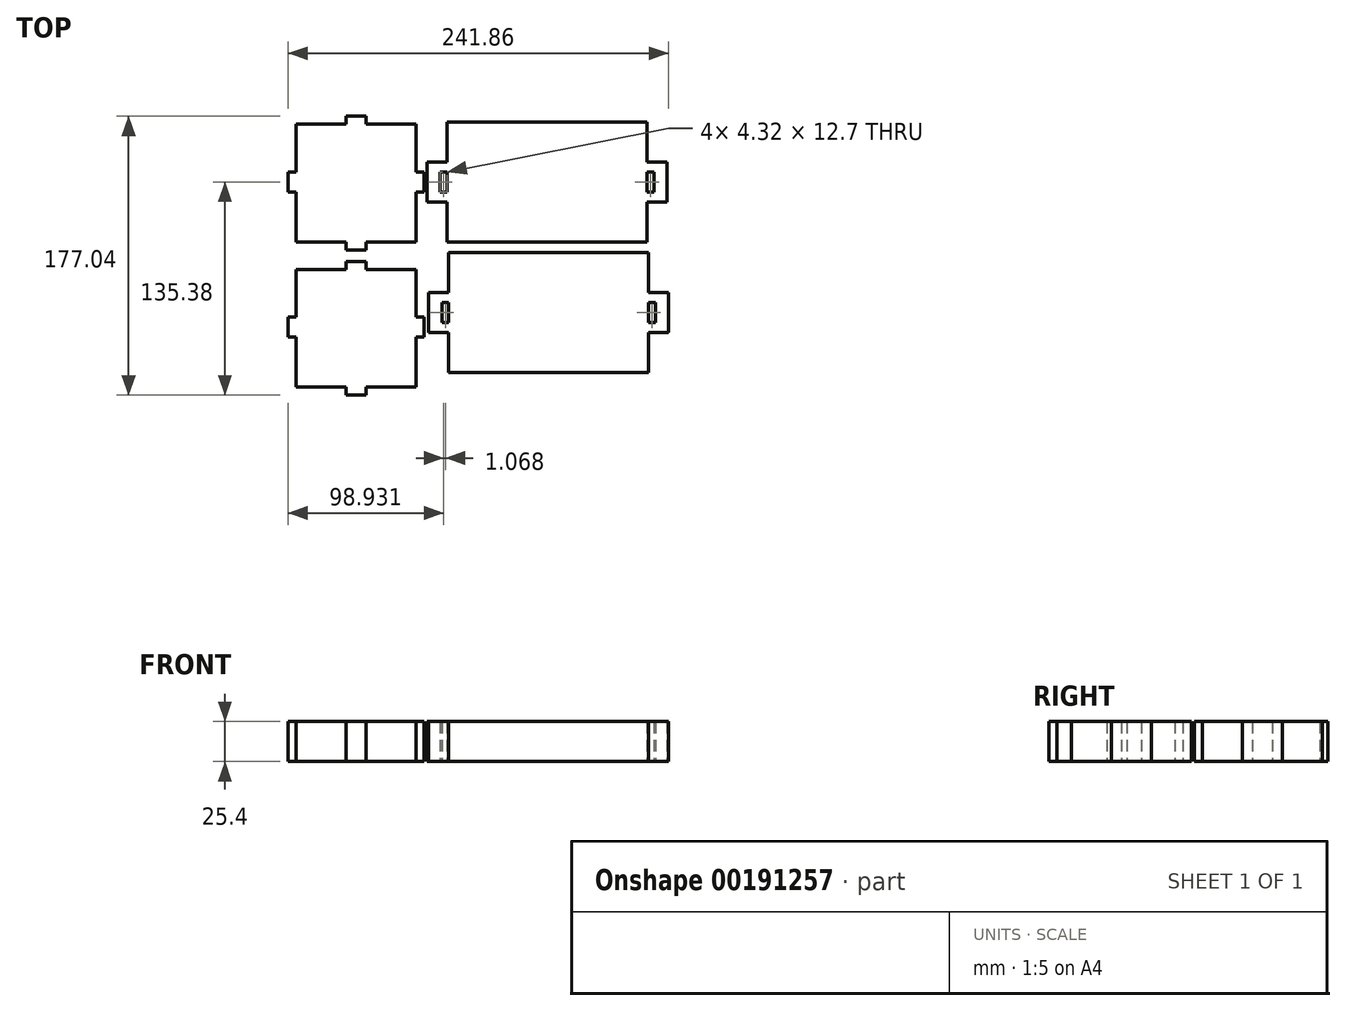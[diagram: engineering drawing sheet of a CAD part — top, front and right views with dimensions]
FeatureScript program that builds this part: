
annotation { "Feature Type Name" : "Feature", "Feature Type Description" : "" }
export const myFeature = defineFeature(function(context is Context, id is Id, definition is map)
    precondition{}
    {
        {
            var Q0;
            Q0=qCreatedBy(makeId("Top.planeOp"),FACE);
            var sketch = newSketch(context, id + "F0", { "sketchPlane" : qUnion([Q0])});
            skLineSegment(sketch, "E0.top", {"start": v(-63.5, 38.1) * mm, "end": v(63.5, 38.1) * mm});
            skPoint(sketch, "E1.0.1.0", {"position": v(-63.5, 88.9) * mm});
            skPoint(sketch, "E1.0.1.1", {"position": v(-76.2, 63.5) * mm});
            skPoint(sketch, "E1.0.1.2", {"position": v(69.85, 63.5) * mm});
            skPoint(sketch, "E1.0.1.3", {"position": v(-76.2, 76.2) * mm});
            skPoint(sketch, "E1.0.1.5", {"position": v(76.2, 76.2) * mm});
            skLineSegment(sketch, "E1.0.1.6", {"start": v(-63.5, 38.1) * mm, "end": v(-63.5, 114.3) * mm});
            skLineSegment(sketch, "E1.0.1.7", {"start": v(63.5, 38.1) * mm, "end": v(63.5, 114.3) * mm});
            skPoint(sketch, "E1.0.1.8", {"position": v(66.04, 69.85) * mm});
            skPoint(sketch, "E1.0.1.9", {"position": v(63.5, 76.2) * mm});
            skPoint(sketch, "E1.0.1.10", {"position": v(-73.15, 88.9) * mm});
            skLineSegment(sketch, "E1.0.1.11", {"start": v(-63.5, 63.5) * mm, "end": v(-76.2, 63.5) * mm});
            skPoint(sketch, "E1.0.1.12", {"position": v(0, 76.2) * mm});
            skLineSegment(sketch, "E1.0.1.13", {"start": v(63.5, 88.9) * mm, "end": v(76.2, 88.9) * mm});
            skLineSegment(sketch, "E1.0.1.14", {"start": v(-63.5, 114.3) * mm, "end": v(63.5, 114.3) * mm});
            skLineSegment(sketch, "E1.0.1.15", {"start": v(69.85, 82.55) * mm, "end": v(69.85, 69.85) * mm});
            skPoint(sketch, "E1.0.1.16", {"position": v(76.2, 88.9) * mm});
            skPoint(sketch, "E1.0.1.17", {"position": v(-63.5, 76.2) * mm});
            skPoint(sketch, "E1.0.1.18", {"position": v(63.5, 88.9) * mm});
            skPoint(sketch, "E1.0.1.19", {"position": v(76.2, 63.5) * mm});
            skLineSegment(sketch, "E1.0.1.20", {"start": v(-69.85, 82.55) * mm, "end": v(-69.85, 69.85) * mm});
            skPoint(sketch, "E1.0.1.21", {"position": v(76.2, 76.2) * mm});
            skLineSegment(sketch, "E1.0.1.22", {"start": v(-63.5, 114.3) * mm, "end": v(63.5, 114.3) * mm});
            skLineSegment(sketch, "E1.0.1.23", {"start": v(76.2, 88.9) * mm, "end": v(76.2, 63.5) * mm});
            skLineSegment(sketch, "E1.0.1.24", {"start": v(-76.2, 88.9) * mm, "end": v(-76.2, 63.5) * mm});
            skPoint(sketch, "E1.0.1.25", {"position": v(-69.85, 88.9) * mm});
            skPoint(sketch, "E1.0.1.26", {"position": v(63.5, 76.2) * mm});
            skLineSegment(sketch, "E1.0.1.27", {"start": v(63.5, 63.5) * mm, "end": v(76.2, 63.5) * mm});
            skLineSegment(sketch, "E1.0.1.28", {"start": v(-63.5, 76.2) * mm, "end": v(-63.5, 69.85) * mm});
            skLineSegment(sketch, "E1.0.1.29", {"start": v(-63.5, 82.55) * mm, "end": v(-69.85, 82.55) * mm});
            skLineSegment(sketch, "E1.0.1.30", {"start": v(-63.5, 69.85) * mm, "end": v(-69.85, 69.85) * mm});
            skLineSegment(sketch, "E1.0.1.31", {"start": v(-63.5, 88.9) * mm, "end": v(-76.2, 88.9) * mm});
            skLineSegment(sketch, "E1.0.1.32", {"start": v(-63.5, 88.9) * mm, "end": v(-63.5, 63.5) * mm});
            skLineSegment(sketch, "E1.0.1.33", {"start": v(63.5, 76.2) * mm, "end": v(63.5, 82.55) * mm});
            skLineSegment(sketch, "E1.0.1.34", {"start": v(63.5, 69.85) * mm, "end": v(69.85, 69.85) * mm});
            skLineSegment(sketch, "E1.0.1.35", {"start": v(63.5, 82.55) * mm, "end": v(69.85, 82.55) * mm});
            skLineSegment(sketch, "E1.0.1.36", {"start": v(63.5, 88.9) * mm, "end": v(63.5, 63.5) * mm});
            skLineSegment(sketch, "E1.0.1.37", {"start": v(63.5, 82.55) * mm, "end": v(63.5, 69.85) * mm});
            skLineSegment(sketch, "E1.0.1.38", {"start": v(-63.5, 76.2) * mm, "end": v(-63.5, 82.55) * mm});
            skLineSegment(sketch, "E1.0.1.39", {"start": v(-63.5, 82.55) * mm, "end": v(-63.5, 69.85) * mm});
            skPoint(sketch, "E2", {"position": v(76.2, 82.55) * mm});
            skPoint(sketch, "E3", {"position": v(68.26, 82.55) * mm});
            skLineSegment(sketch, "E4", {"start": v(68.26, 69.85) * mm, "end": v(69.85, 69.85) * mm});
            skPoint(sketch, "E5", {"position": v(67.82, 82.55) * mm});
            skLineSegment(sketch, "E6.top", {"start": v(71.1, 69.85) * mm, "end": v(66.04, 69.85) * mm});
            skLineSegment(sketch, "E7", {"start": v(67.82, 82.55) * mm, "end": v(67.82, 69.85) * mm});
            skPoint(sketch, "E8", {"position": v(-67.82, 69.85) * mm});
            skLineSegment(sketch, "E9", {"start": v(-67.82, 69.85) * mm, "end": v(-67.82, 82.55) * mm});
            skPoint(sketch, "E10", {"position": v(-78.23, 88.9) * mm});
            skPoint(sketch, "E11", {"position": v(-78.23, 82.55) * mm});
            skPoint(sketch, "E12", {"position": v(-78.23, 69.85) * mm});
            skPoint(sketch, "E13", {"position": v(-83.31, 82.55) * mm});
            skLineSegment(sketch, "E14.bottom", {"start": v(-83.31, 82.55) * mm, "end": v(-78.23, 82.55) * mm});
            skLineSegment(sketch, "E14.top", {"start": v(-83.31, 69.85) * mm, "end": v(-78.23, 69.85) * mm});
            skLineSegment(sketch, "E14.left", {"start": v(-83.31, 82.55) * mm, "end": v(-83.31, 69.85) * mm});
            skLineSegment(sketch, "E14.right", {"start": v(-78.23, 82.55) * mm, "end": v(-78.23, 69.85) * mm});
            skPoint(sketch, "E15", {"position": v(-170.57, 59.84) * mm});
            skLineSegment(sketch, "E16.bottom", {"start": v(-83.31, 38.1) * mm, "end": v(-159.51, 38.1) * mm});
            skLineSegment(sketch, "E16.top", {"start": v(-83.31, 112.78) * mm, "end": v(-159.51, 112.78) * mm});
            skLineSegment(sketch, "E16.left", {"start": v(-83.31, 38.1) * mm, "end": v(-83.31, 112.78) * mm});
            skLineSegment(sketch, "E16.right", {"start": v(-159.51, 38.1) * mm, "end": v(-159.51, 112.78) * mm});
            skPoint(sketch, "E17", {"position": v(-115.06, 38.1) * mm});
            skPoint(sketch, "E18", {"position": v(-127.76, 38.1) * mm});
            skLineSegment(sketch, "E19", {"start": v(-127.76, 38.1) * mm, "end": v(-127.76, 33.02) * mm});
            skLineSegment(sketch, "E20", {"start": v(-127.76, 33.02) * mm, "end": v(-115.06, 33.02) * mm});
            skLineSegment(sketch, "E21", {"start": v(-115.06, 33.02) * mm, "end": v(-115.06, 38.1) * mm});
            skPoint(sketch, "E22", {"position": v(-159.51, 69.85) * mm});
            skPoint(sketch, "E23", {"position": v(-159.51, 82.55) * mm});
            skLineSegment(sketch, "E24", {"start": v(-159.51, 82.55) * mm, "end": v(-164.6, 82.55) * mm});
            skLineSegment(sketch, "E25", {"start": v(-164.6, 82.55) * mm, "end": v(-164.6, 69.85) * mm});
            skLineSegment(sketch, "E26", {"start": v(-164.6, 69.85) * mm, "end": v(-159.51, 69.85) * mm});
            skPoint(sketch, "E27", {"position": v(-127.76, 112.78) * mm});
            skPoint(sketch, "E28", {"position": v(-115.06, 112.78) * mm});
            skPoint(sketch, "E29", {"position": v(-127.76, 117.86) * mm});
            skLineSegment(sketch, "E30.bottom", {"start": v(-115.06, 112.78) * mm, "end": v(-127.76, 112.78) * mm});
            skLineSegment(sketch, "E30.top", {"start": v(-115.06, 117.86) * mm, "end": v(-127.76, 117.86) * mm});
            skLineSegment(sketch, "E30.left", {"start": v(-115.06, 112.78) * mm, "end": v(-115.06, 117.86) * mm});
            skLineSegment(sketch, "E30.right", {"start": v(-127.76, 112.78) * mm, "end": v(-127.76, 117.86) * mm});
            skLineSegment(sketch, "E31.direction1", {"start": v(-159.51, 38.1) * mm, "end": v(-134.11, 38.1) * mm, "construction": true});
            skPoint(sketch, "E32.0.1.0", {"position": v(68.89, -0.5) * mm});
            skPoint(sketch, "E32.0.1.1", {"position": v(70.92, -19.55) * mm});
            skPoint(sketch, "E32.0.1.2", {"position": v(77.27, -19.55) * mm});
            skPoint(sketch, "E32.0.1.3", {"position": v(67.1, -13.2) * mm});
            skPoint(sketch, "E32.0.1.4", {"position": v(-68.78, 5.85) * mm});
            skPoint(sketch, "E32.0.1.5", {"position": v(-72.08, 5.85) * mm});
            skLineSegment(sketch, "E32.0.1.6", {"start": v(-62.43, -44.95) * mm, "end": v(64.57, -44.95) * mm});
            skLineSegment(sketch, "E32.0.1.7", {"start": v(64.57, -44.95) * mm, "end": v(64.57, 31.25) * mm});
            skLineSegment(sketch, "E32.0.1.8", {"start": v(-62.43, -19.55) * mm, "end": v(-75.13, -19.55) * mm});
            skPoint(sketch, "E32.0.1.9", {"position": v(64.57, 5.85) * mm});
            skPoint(sketch, "E32.0.1.11", {"position": v(-75.13, -6.85) * mm});
            skLineSegment(sketch, "E32.0.1.12", {"start": v(-68.78, -0.5) * mm, "end": v(-68.78, -13.2) * mm});
            skLineSegment(sketch, "E32.0.1.13", {"start": v(-62.43, 31.25) * mm, "end": v(64.57, 31.25) * mm});
            skLineSegment(sketch, "E32.0.1.14", {"start": v(77.27, 5.85) * mm, "end": v(77.27, -19.55) * mm});
            skLineSegment(sketch, "E32.0.1.15", {"start": v(-75.13, 5.85) * mm, "end": v(-75.13, -19.55) * mm});
            skPoint(sketch, "E32.0.1.16", {"position": v(64.57, -6.85) * mm});
            skPoint(sketch, "E32.0.1.17", {"position": v(77.27, -0.5) * mm});
            skPoint(sketch, "E32.0.1.18", {"position": v(77.27, -6.85) * mm});
            skPoint(sketch, "E32.0.1.19", {"position": v(-62.43, 5.85) * mm});
            skPoint(sketch, "E32.0.1.20", {"position": v(69.33, -0.5) * mm});
            skPoint(sketch, "E32.0.1.21", {"position": v(-75.13, -19.55) * mm});
            skLineSegment(sketch, "E32.0.1.22", {"start": v(-62.43, -44.95) * mm, "end": v(-62.43, 31.25) * mm});
            skPoint(sketch, "E32.0.1.23", {"position": v(1.07, -6.85) * mm});
            skPoint(sketch, "E32.0.1.24", {"position": v(77.27, 5.85) * mm});
            skPoint(sketch, "E32.0.1.25", {"position": v(-62.43, -6.85) * mm});
            skLineSegment(sketch, "E32.0.1.26", {"start": v(64.57, -19.55) * mm, "end": v(77.27, -19.55) * mm});
            skLineSegment(sketch, "E32.0.1.27", {"start": v(64.57, 5.85) * mm, "end": v(77.27, 5.85) * mm});
            skLineSegment(sketch, "E32.0.1.28", {"start": v(-62.43, 31.25) * mm, "end": v(64.57, 31.25) * mm});
            skLineSegment(sketch, "E32.0.1.29", {"start": v(-62.43, -44.95) * mm, "end": v(64.57, -44.95) * mm});
            skPoint(sketch, "E32.0.1.30", {"position": v(64.57, -6.85) * mm});
            skPoint(sketch, "E32.0.1.31", {"position": v(77.27, -6.85) * mm});
            skLineSegment(sketch, "E32.0.1.32", {"start": v(-62.43, 5.85) * mm, "end": v(-75.13, 5.85) * mm});
            skLineSegment(sketch, "E32.0.1.33", {"start": v(-62.43, 5.85) * mm, "end": v(-62.43, -19.55) * mm});
            skLineSegment(sketch, "E32.0.1.34", {"start": v(64.57, 5.85) * mm, "end": v(64.57, -19.55) * mm});
            skLineSegment(sketch, "E32.0.1.35", {"start": v(-62.43, -44.95) * mm, "end": v(64.57, -44.95) * mm});
            skLineSegment(sketch, "E32.0.1.36", {"start": v(70.92, -0.5) * mm, "end": v(70.92, -13.2) * mm});
            skLineSegment(sketch, "E32.0.1.37", {"start": v(-62.43, -13.2) * mm, "end": v(-68.78, -13.2) * mm});
            skLineSegment(sketch, "E32.0.1.38", {"start": v(-62.43, -0.5) * mm, "end": v(-62.43, -13.2) * mm});
            skLineSegment(sketch, "E32.0.1.39", {"start": v(68.89, -0.5) * mm, "end": v(68.89, -13.2) * mm});
            skLineSegment(sketch, "E32.0.1.40", {"start": v(64.57, -0.5) * mm, "end": v(70.92, -0.5) * mm});
            skLineSegment(sketch, "E32.0.1.41", {"start": v(-62.43, -0.5) * mm, "end": v(-68.78, -0.5) * mm});
            skLineSegment(sketch, "E32.0.1.43", {"start": v(64.57, -0.5) * mm, "end": v(64.57, -13.2) * mm});
            skLineSegment(sketch, "E32.0.1.44", {"start": v(64.57, -6.85) * mm, "end": v(64.57, -0.5) * mm});
            skLineSegment(sketch, "E32.0.1.45", {"start": v(-62.43, -6.85) * mm, "end": v(-62.43, -0.5) * mm});
            skLineSegment(sketch, "E32.0.1.46", {"start": v(72.16, -13.2) * mm, "end": v(67.1, -13.2) * mm});
            skLineSegment(sketch, "E32.0.1.47", {"start": v(64.57, -13.2) * mm, "end": v(70.92, -13.2) * mm});
            skLineSegment(sketch, "E32.0.1.48", {"start": v(-62.43, -6.85) * mm, "end": v(-62.43, -13.2) * mm});
            skLineSegment(sketch, "E32.0.1.49", {"start": v(69.33, -13.2) * mm, "end": v(70.92, -13.2) * mm});
            skLineSegment(sketch, "E32.direction1", {"start": v(-63.5, 38.1) * mm, "end": v(-38.1, 38.1) * mm, "construction": true});
            skLineSegment(sketch, "E32.direction2", {"start": v(-63.5, 38.1) * mm, "end": v(-62.43, -44.95) * mm, "construction": true});
            skPoint(sketch, "E33", {"position": v(-65.6, -0.5) * mm});
            skPoint(sketch, "E34", {"position": v(-66.75, -13.2) * mm});
            skLineSegment(sketch, "E35", {"start": v(-66.75, -13.2) * mm, "end": v(-66.75, -0.5) * mm});
            skLineSegment(sketch, "E36.0.1.0", {"start": v(-83.31, -54.1) * mm, "end": v(-83.31, 20.57) * mm});
            skLineSegment(sketch, "E36.0.1.1", {"start": v(-115.06, 25.65) * mm, "end": v(-127.76, 25.65) * mm});
            skLineSegment(sketch, "E36.0.1.2", {"start": v(-159.51, -54.1) * mm, "end": v(-159.51, 20.57) * mm});
            skPoint(sketch, "E36.0.1.3", {"position": v(-127.76, -54.1) * mm});
            skLineSegment(sketch, "E36.0.1.4", {"start": v(-83.31, -9.65) * mm, "end": v(-83.31, -22.35) * mm});
            skLineSegment(sketch, "E36.0.1.5", {"start": v(-159.51, -54.1) * mm, "end": v(-134.11, -54.1) * mm, "construction": true});
            skPoint(sketch, "E36.0.1.6", {"position": v(-83.31, -9.65) * mm});
            skLineSegment(sketch, "E36.0.1.7", {"start": v(-83.31, 20.57) * mm, "end": v(-159.51, 20.57) * mm});
            skPoint(sketch, "E36.0.1.8", {"position": v(-159.51, -22.35) * mm});
            skPoint(sketch, "E36.0.1.9", {"position": v(-115.06, -54.1) * mm});
            skPoint(sketch, "E36.0.1.10", {"position": v(-159.51, -9.65) * mm});
            skLineSegment(sketch, "E36.0.1.11", {"start": v(-83.31, -54.1) * mm, "end": v(-159.51, -54.1) * mm});
            skLineSegment(sketch, "E36.0.1.12", {"start": v(-115.06, 20.57) * mm, "end": v(-127.76, 20.57) * mm});
            skPoint(sketch, "E36.0.1.13", {"position": v(-127.76, 20.57) * mm});
            skLineSegment(sketch, "E36.0.1.14", {"start": v(-127.76, -59.18) * mm, "end": v(-115.06, -59.18) * mm});
            skPoint(sketch, "E36.0.1.15", {"position": v(-115.06, 20.57) * mm});
            skLineSegment(sketch, "E36.0.1.16", {"start": v(-78.23, -9.65) * mm, "end": v(-78.23, -22.35) * mm});
            skLineSegment(sketch, "E36.0.1.17", {"start": v(-164.6, -9.65) * mm, "end": v(-164.6, -22.35) * mm});
            skLineSegment(sketch, "E36.0.1.18", {"start": v(-164.6, -22.35) * mm, "end": v(-159.51, -22.35) * mm});
            skLineSegment(sketch, "E36.0.1.19", {"start": v(-159.51, -9.65) * mm, "end": v(-164.6, -9.65) * mm});
            skLineSegment(sketch, "E36.0.1.20", {"start": v(-115.06, -59.18) * mm, "end": v(-115.06, -54.1) * mm});
            skLineSegment(sketch, "E36.0.1.21", {"start": v(-127.76, -54.1) * mm, "end": v(-127.76, -59.18) * mm});
            skLineSegment(sketch, "E36.0.1.22", {"start": v(-115.06, 20.57) * mm, "end": v(-115.06, 25.65) * mm});
            skLineSegment(sketch, "E36.0.1.23", {"start": v(-127.76, 20.57) * mm, "end": v(-127.76, 25.65) * mm});
            skLineSegment(sketch, "E36.0.1.24", {"start": v(-83.31, -22.35) * mm, "end": v(-78.23, -22.35) * mm});
            skLineSegment(sketch, "E36.0.1.25", {"start": v(-83.31, -9.65) * mm, "end": v(-78.23, -9.65) * mm});
            skPoint(sketch, "E36.0.1.26", {"position": v(-78.23, -9.65) * mm});
            skPoint(sketch, "E36.0.1.27", {"position": v(-78.23, -22.35) * mm});
            skPoint(sketch, "E36.0.1.28", {"position": v(-127.76, 25.65) * mm});
            skLineSegment(sketch, "E36.direction2", {"start": v(-159.51, 38.1) * mm, "end": v(-159.51, -54.1) * mm, "construction": true});
            skSolve(sketch);
        }
        {
            var Q0;
            Q0 = qSketchRegion(id + "F0", true);
            var Q1;
            {var subQ0=sQuery(id+"F0.wireOp",EDGE,"E32.0.1.12");Q1=makeQuery(id+"F0.imprint","IMPRINT",FACE,{"disambiguationData":[TD([[makeQuery(id+"F0.imprint","IMPRINT",EDGE,{"derivedFrom":subQ0}),1.0]])]});}
            var Q2;
            {var subQ1=sQuery(id+"F0.wireOp",EDGE,"E32.0.1.36");Q2=makeQuery(id+"F0.imprint","IMPRINT",FACE,{"disambiguationData":[TD([[makeQuery(id+"F0.imprint","IMPRINT",EDGE,{"derivedFrom":subQ1}),-1.0]])]});}
            var Q3;
            {var subQ4=sQuery(id+"F0.wireOp",EDGE,"E1.0.1.15");Q3=makeQuery(id+"F0.imprint","IMPRINT",FACE,{"disambiguationData":[TD([[makeQuery(id+"F0.imprint","IMPRINT",EDGE,{"derivedFrom":subQ4}),-1.0]])]});}
            var Q4;
            {var subQ0=sQuery(id+"F0.wireOp",EDGE,"E1.0.1.20");Q4=makeQuery(id+"F0.imprint","IMPRINT",FACE,{"disambiguationData":[TD([[makeQuery(id+"F0.imprint","IMPRINT",EDGE,{"derivedFrom":subQ0}),1.0]])]});}
            extrude(context, id + "F1", {"entities" : qUnion([Q0, Q1, Q2, Q3, Q4]), "depth" : 25.4 * mm});
        }
    });
